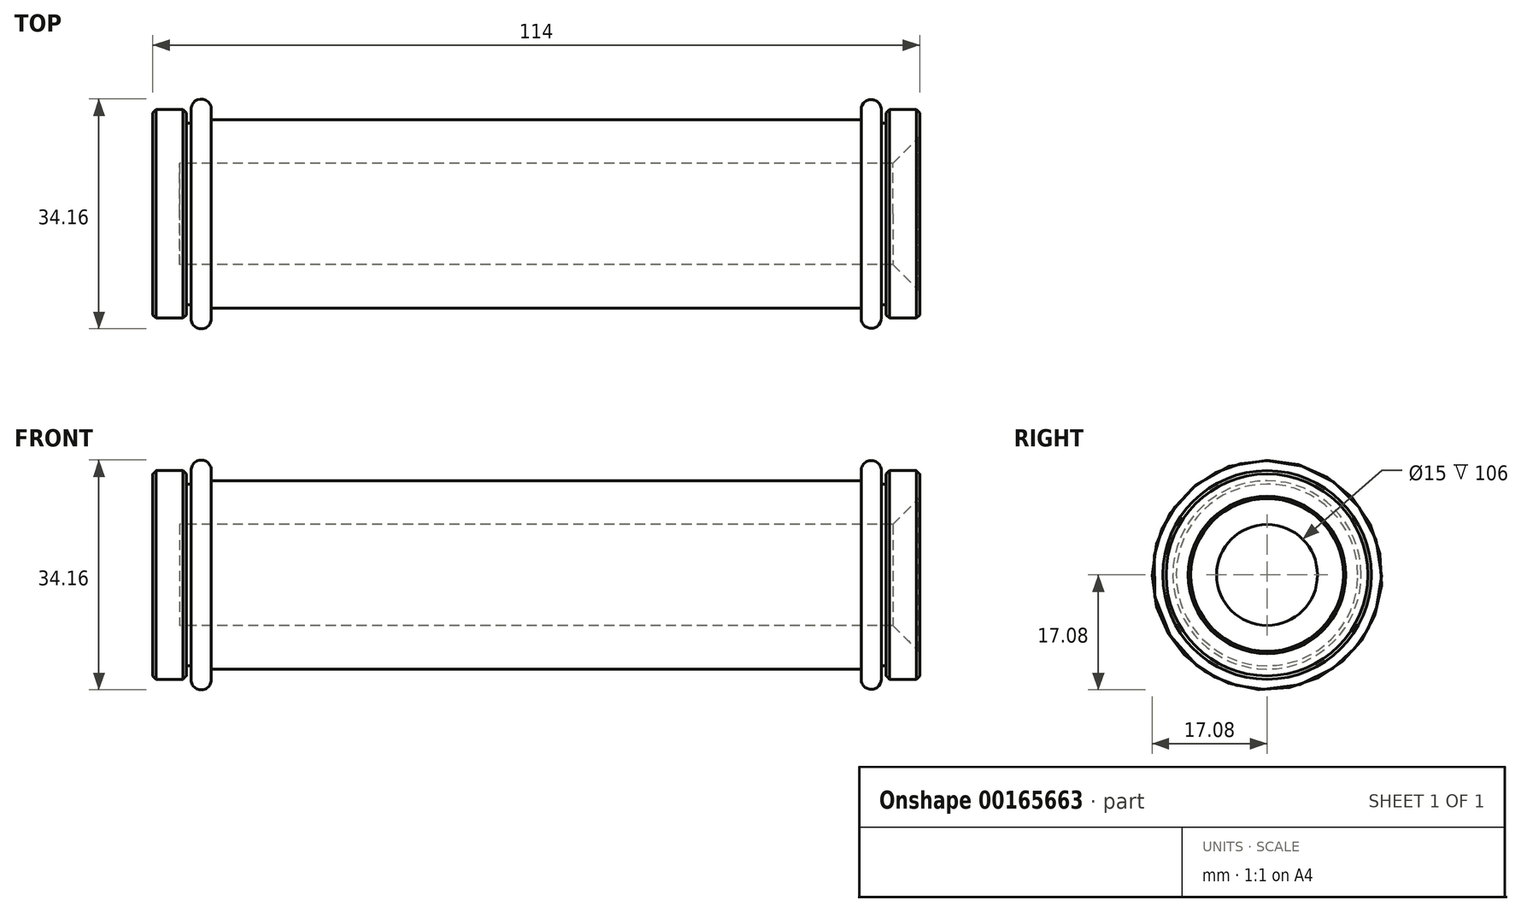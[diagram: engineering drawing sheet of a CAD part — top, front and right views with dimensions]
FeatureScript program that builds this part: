
annotation { "Feature Type Name" : "Feature", "Feature Type Description" : "" }
export const myFeature = defineFeature(function(context is Context, id is Id, definition is map)
    precondition{}
    {
        {
            var Q0;
            Q0=qCreatedBy(makeId("Front.planeOp"),FACE);
            var sketch = newSketch(context, id + "F0", { "sketchPlane" : qUnion([Q0]) });
            skLineSegment(sketch, "E0", {"start": v(-55, 7.5) * mm, "end": v(55, 7.5) * mm});
            skPoint(sketch, "E1", {"position": v(0, 7.5) * mm});
            skLineSegment(sketch, "E2", {"start": v(-55, 7.5) * mm, "end": v(-55, 0) * mm});
            skLineSegment(sketch, "E3", {"start": v(-55, 0) * mm, "end": v(-59, 0) * mm});
            skLineSegment(sketch, "E4", {"start": v(-59, 0) * mm, "end": v(-59, 15.5) * mm});
            skLineSegment(sketch, "E5", {"start": v(-59, 15.5) * mm, "end": v(-54, 15.5) * mm});
            skLineSegment(sketch, "E6", {"start": v(-54, 15.5) * mm, "end": v(-54, 13.5) * mm});
            skLineSegment(sketch, "E7", {"start": v(-54, 13.5) * mm, "end": v(-53.3, 13.5) * mm});
            skArc(sketch, "E8", {"start": v(-50.3, 15.5) * mm, "mid": v(-51.8, 17.08) * mm, "end": v(-53.3, 15.5) * mm});
            skLineSegment(sketch, "E9", {"start": v(-53.3, 15.5) * mm, "end": v(-53.3, 13.5) * mm});
            skLineSegment(sketch, "E10", {"start": v(-50.3, 15.5) * mm, "end": v(-50.3, 14) * mm});
            skLineSegment(sketch, "E11", {"start": v(-50.3, 14) * mm, "end": v(46.3, 14) * mm});
            skLineSegment(sketch, "E12", {"start": v(55, 7.5) * mm, "end": v(55, 15.5) * mm});
            skLineSegment(sketch, "E13", {"start": v(55, 15.5) * mm, "end": v(50, 15.5) * mm});
            skLineSegment(sketch, "E14", {"start": v(50, 15.5) * mm, "end": v(50, 13.5) * mm});
            skLineSegment(sketch, "E15", {"start": v(50, 13.5) * mm, "end": v(49.3, 13.5) * mm});
            skLineSegment(sketch, "E16", {"start": v(49.3, 13.5) * mm, "end": v(49.3, 15.5) * mm});
            skLineSegment(sketch, "E17", {"start": v(46.3, 14) * mm, "end": v(46.3, 15.5) * mm});
            skArc(sketch, "E18", {"start": v(49.3, 15.5) * mm, "mid": v(47.8, 17) * mm, "end": v(46.3, 15.5) * mm});
            skLineSegment(sketch, "E19", {"start": v(-77.44, 0) * mm, "end": v(68.42, 0) * mm, "construction": true});
            skSolve(sketch);
        }
        {
            var Q0;
            Q0=makeQuery(id+"F0.imprint","IMPRINT",FACE,{"disambiguationData":[TD([[makeQuery(id+"F0.imprint","IMPRINT",EDGE,{"derivedFrom":sQuery(id+"F0.wireOp",EDGE,"E0")}),1.0]])]});
            var Q1;
            Q1=sQuery(id+"F0.wireOp",EDGE,"E19");
            revolve(context, id + "F1", {"surfaceOperationType" : NewSurfaceOperationType.NEW, "entities" : qUnion([Q0]), "axis" : qUnion([Q1]), "revolveType" : RevolveType.FULL});
        }
        {
            var Q0;
            Q0=makeQuery(id+"F1.opRevolve","SWEPT_EDGE",EDGE,{"disambiguationData":[OSD([sQuery(id+"F0.wireOp",EDGE,"E0"),sQuery(id+"F0.wireOp",EDGE,"E12")])]});
            chamfer(context, id + "F2", {"entities" : qUnion([Q0]), "width" : 4 * mm, "tangentPropagation" : true});
        }
        {
            var Q0;
            Q0=makeQuery(id+"F1.opRevolve","SWEPT_EDGE",EDGE,{"disambiguationData":[OSD([sQuery(id+"F0.wireOp",EDGE,"E12"),sQuery(id+"F0.wireOp",EDGE,"E13")])]});
            var Q1;
            {var subQ0=sQuery(id+"F0.wireOp",EDGE,"E12");Q1=makeQuery(id+"F2.opChamfer","BLEND_EDGE",EDGE,{"blendedFrom":[makeQuery(id+"F1.opRevolve","SWEPT_EDGE",EDGE,{"disambiguationData":[OSD([sQuery(id+"F0.wireOp",EDGE,"E0"),subQ0])]}),makeQuery(id+"F1.opRevolve","SWEPT_FACE",FACE,{"disambiguationData":[OSD([subQ0])]})],"blendedInto":[makeQuery(id+"F1.opRevolve","SWEPT_FACE",FACE,{"disambiguationData":[OSD([subQ0])]})]});}
            var Q2;
            Q2=makeQuery(id+"F1.opRevolve","SWEPT_EDGE",EDGE,{"disambiguationData":[OSD([sQuery(id+"F0.wireOp",EDGE,"E4"),sQuery(id+"F0.wireOp",EDGE,"E5")])]});
            var Q3;
            Q3=makeQuery(id+"F1.opRevolve","SWEPT_EDGE",EDGE,{"disambiguationData":[OSD([sQuery(id+"F0.wireOp",EDGE,"E5"),sQuery(id+"F0.wireOp",EDGE,"E6")])]});
            var Q4;
            Q4=makeQuery(id+"F1.opRevolve","SWEPT_EDGE",EDGE,{"disambiguationData":[OSD([sQuery(id+"F0.wireOp",EDGE,"E13"),sQuery(id+"F0.wireOp",EDGE,"E14")])]});
            chamfer(context, id + "F3", {"entities" : qUnion([Q0, Q1, Q2, Q3, Q4]), "width" : 0.5 * mm, "tangentPropagation" : true});
        }
    });
